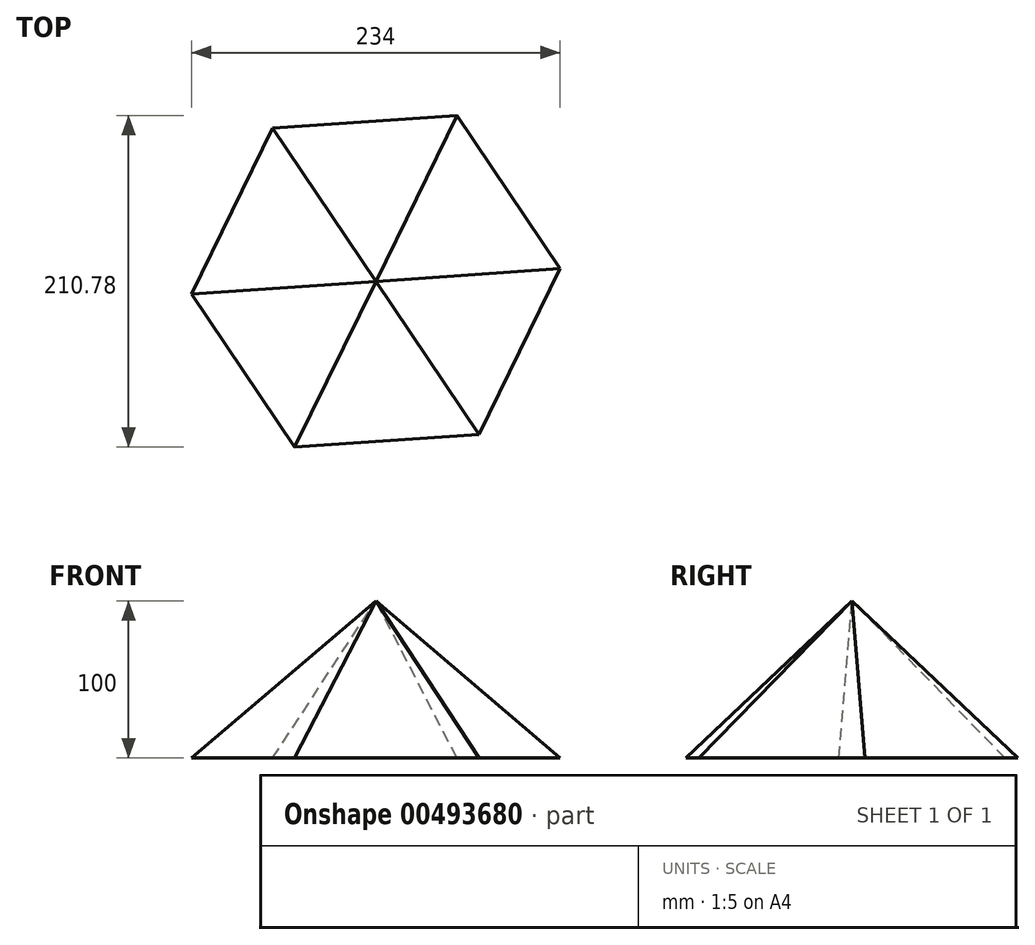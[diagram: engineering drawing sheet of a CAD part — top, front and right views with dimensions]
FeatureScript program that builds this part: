
annotation { "Feature Type Name" : "Feature", "Feature Type Description" : "" }
export const myFeature = defineFeature(function(context is Context, id is Id, definition is map)
    precondition{}
    {
        {
            var Q0;
            Q0=qCreatedBy(makeId("Top.planeOp"),FACE);
            var sketch = newSketch(context, id + "F0", { "sketchPlane" : qUnion([Q0])});
            skCircle(sketch, "E0.cCircle", {"center": v(0, 0) * mm, "radius": 117.28 * mm, "construction": true});
            skLineSegment(sketch, "E0.0", {"start": v(117, 8.12) * mm, "end": v(65.53, -97.27) * mm});
            skLineSegment(sketch, "E0.1", {"start": v(65.53, -97.27) * mm, "end": v(-51.47, -105.39) * mm});
            skLineSegment(sketch, "E0.2", {"start": v(-51.47, -105.39) * mm, "end": v(-117, -8.12) * mm});
            skLineSegment(sketch, "E0.3", {"start": v(-117, -8.12) * mm, "end": v(-65.53, 97.27) * mm});
            skLineSegment(sketch, "E0.4", {"start": v(-65.53, 97.27) * mm, "end": v(51.47, 105.39) * mm});
            skLineSegment(sketch, "E0.5", {"start": v(51.47, 105.39) * mm, "end": v(117, 8.12) * mm});
            skSolve(sketch);
        }
        {
            var Q0;
            Q0=qCreatedBy(makeId("Top.planeOp"),FACE);
            cPlane(context, id + "F1", {"entities" : qUnion([Q0]), "cplaneType" : CPlaneType.OFFSET, "offset" : 100 * mm, "width" : 150 * mm, "height" : 150 * mm});
        }
        {
            var Q0;
            Q0=qCreatedBy(id+"F1.planeOp",FACE);
            var sketch = newSketch(context, id + "F2", { "sketchPlane" : qUnion([Q0])});
            skPoint(sketch, "E1", {"position": v(0, 0) * mm});
            skSolve(sketch);
        }
        {
            var Q0;
            Q0=makeQuery(id+"F0.imprint","IMPRINT",FACE,{"disambiguationData":[TD([[makeQuery(id+"F0.imprint","IMPRINT",EDGE,{"derivedFrom":sQuery(id+"F0.wireOp",EDGE,"E0.0")}),-1.0]])]});
            var Q1;
            Q1=sQuery(id+"F2.wireOp",VERTEX,"E1");
            loft(context, id + "F3", {"sheetProfilesArray" : [{ "sheetProfileEntities" : qUnion([Q0]) }, { "sheetProfileEntities" : qUnion([Q1]) }]});
        }
    });
